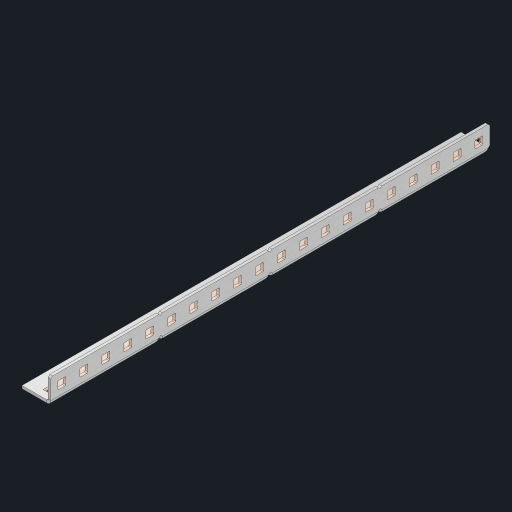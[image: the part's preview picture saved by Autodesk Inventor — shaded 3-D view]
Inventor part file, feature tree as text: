
AUTODESK INVENTOR PART (.ipt)
format: ipt  version: 2023 (Build 270158000, 158)  size: 776,192 bytes
history: native  units: in
note: dims shown in document units (in); Inventor stores cm internally (conversion verified against a paired STEP export)
features: other x45, extrude x39, sheet_metal_op x10, sketch x8, mirror x1, pattern_linear x1, chamfer x1
ambient origin geometry x8: Origin, YZ Plane, XZ Plane, XY Plane, X Axis, Y Axis, Z Axis, Center Point
bodies: Solid1 (feature_tree), Body (feature_tree)
feature tree (105):
  other  "Flange Pattern Plane"
  sheet_metal_op  "Flange Pattern"
  sheet_metal_op  "Body Pattern"
  other  "Arc Length"
  mirror  "Notch Mirror"
  pattern_linear  "Notch Pattern"  Spacing1=0.25in  [1 undecoded]
  chamfer  "End Chamfer"
  extrude  "Half Cut"  Depth=0.0625in
  sketch  "Sketch1"  dims[d0=1.5in]
  other  "Plate1"
  sketch  "Sketch2"  dims[d1=10.0in]
  other  "Plate2"
  sheet_metal_op  "Bend1"
  sheet_metal_op  "Corner1"
  sketch  "Sketch3"  dims[d2=0.0625in]
  other  "Flange Pattern Sketch"
  sketch  "Sketch7"  dims[d3=0.0625in]
  other  "Srf1"
  other  "Srf2"
  sketch  "Sketch8"  dims[d4=0.0312in]
  sketch  "Sketch9"  dims[d5=0.125in]
  other  "Srf91"
  sheet_metal_op  "Body Pattern Sketch"
  other  "Srf92"
  sketch  "Sketch13"  dims[d6=0.0625in]
  sketch  "Sketch14"  dims[d7=0.5in d8=90.0deg d9=0.0312in d10=0.25in d11=0.0625in d12=0.0625in d16=0.182in d17=0.02in d18=0.0625in d19=0.0in d20=0.25in d21=0.25in d46=0.172in d47=1.0in d48=0.0in d49=0.182in d50=0.02in d51=0.25in d52=0.25in d53=0.0625in d54=0.0in d55=0.172in d56=1.0in d57=0.0in d60=7.874in d62=0.5in d63=0.3937in d65=0.5in d85=0.1473in d86=0.1782in d88=0.04in d89=0.0625in d90=0.0in d91=0.04in d92=0.0491in d95=2.5in d96=0.04in d97=0.25in d98=45.0deg d101=0.0in d102=2.497in d131=0.5in d132=7.874in d134=0.5in d139=0.5in]
  other  "Srf856"
  other  "Srf1310"
  other  "Srf1311"
  other  "Srf1312"
  other  "Srf1376"
  other  "Srf1377"
  other  "Srf1728"
  other  "Srf1755"
  other  "Srf1878"
  other  "Srf1879"
  other  "Srf1880"
  other  "Srf1881"
  other  "Srf1882"
  other  "Srf1883"
  other  "Srf1884"
  other  "Srf1885"
  other  "Srf1886"
  other  "Srf1887"
  other  "Srf1888"
  other  "Srf1889"
  other  "Srf1890"
  other  "Srf1891"
  other  "Srf1942"
  other  "Srf1943"
  other  "Srf1944"
  other  "Srf1945"
  other  "Srf1946"
  other  "Srf1947"
  other  "Srf1948"
  other  "Srf1949"
  other  "Srf1950"
  other  "Srf1951"
  other  "Srf1952"
  other  "Srf1953"
  other  "Srf1954"
  other  "Srf1955"
  sheet_metal_op  "Flange Stamp"
  sheet_metal_op  "Flange Circle"
  sheet_metal_op  "Body Stamp"
  sheet_metal_op  "Body Circle"
  sheet_metal_op  "Notch"
  extrude  "ExtrusionSrf2"  Depth=0.0625in
  extrude  "ExtrusionSrf92"  Depth=0.0625in
  extrude  "ExtrusionSrf856"  Depth=0.02in
  extrude  "ExtrusionSrf1310"  Depth=0.0625in
  extrude  "ExtrusionSrf1311"  TaperAngle=0.0deg  [1 undecoded]
  extrude  "ExtrusionSrf1312"  Depth=0.0625in
  extrude  "ExtrusionSrf1376"  Depth=0.0625in
  extrude  "ExtrusionSrf1377"  Depth=0.0625in
  extrude  "ExtrusionSrf1728"  Depth=0.0625in TaperAngle=0.0deg
  extrude  "ExtrusionSrf1755"  Depth=0.0625in
  extrude  "ExtrusionSrf1878"  Depth=0.02in
  extrude  "ExtrusionSrf1879"  Depth=0.0625in
  extrude  "ExtrusionSrf1880"  Depth=0.0625in
  extrude  "ExtrusionSrf1881"  Depth=0.0625in
  extrude  "ExtrusionSrf1882"  TaperAngle=0.0deg  [1 undecoded]
  extrude  "ExtrusionSrf1883"  Depth=0.0625in
  extrude  "ExtrusionSrf1884"  Depth=0.0625in TaperAngle=0.0deg
  extrude  "ExtrusionSrf1885"  Depth=0.0625in
  extrude  "ExtrusionSrf1886"  Depth=0.3937in
  extrude  "ExtrusionSrf1887"  Depth=0.0625in
  extrude  "ExtrusionSrf1888"  Depth=0.0625in
  extrude  "ExtrusionSrf1889"  Depth=0.0625in
  extrude  "ExtrusionSrf1890"  Depth=0.0625in
  extrude  "ExtrusionSrf1891"  TaperAngle=0.0deg  [1 undecoded]
  extrude  "ExtrusionSrf1942"  Depth=0.0625in
  extrude  "ExtrusionSrf1943"  Depth=0.0625in
  extrude  "ExtrusionSrf1944"  Depth=0.0625in
  extrude  "ExtrusionSrf1945"  Depth=0.0625in TaperAngle=45.0deg
  extrude  "ExtrusionSrf1946"  TaperAngle=0.0deg  [1 undecoded]
  extrude  "ExtrusionSrf1947"  Depth=0.0625in
  extrude  "ExtrusionSrf1948"  Depth=0.0625in
  extrude  "ExtrusionSrf1949"  Depth=0.0625in
  extrude  "ExtrusionSrf1950"  Depth=0.0625in
  extrude  "ExtrusionSrf1951"  Depth=0.0625in
  extrude  "ExtrusionSrf1952"  [1 undecoded]
  extrude  "ExtrusionSrf1953"  [1 undecoded]
  extrude  "ExtrusionSrf1954"  [1 undecoded]
  extrude  "ExtrusionSrf1955"  [1 undecoded]
note: 9 required parameter values undecoded (feature->parameter linkage not recoverable at this tier; creation-order binding heuristic only, values carry confidence <= 0.55)
